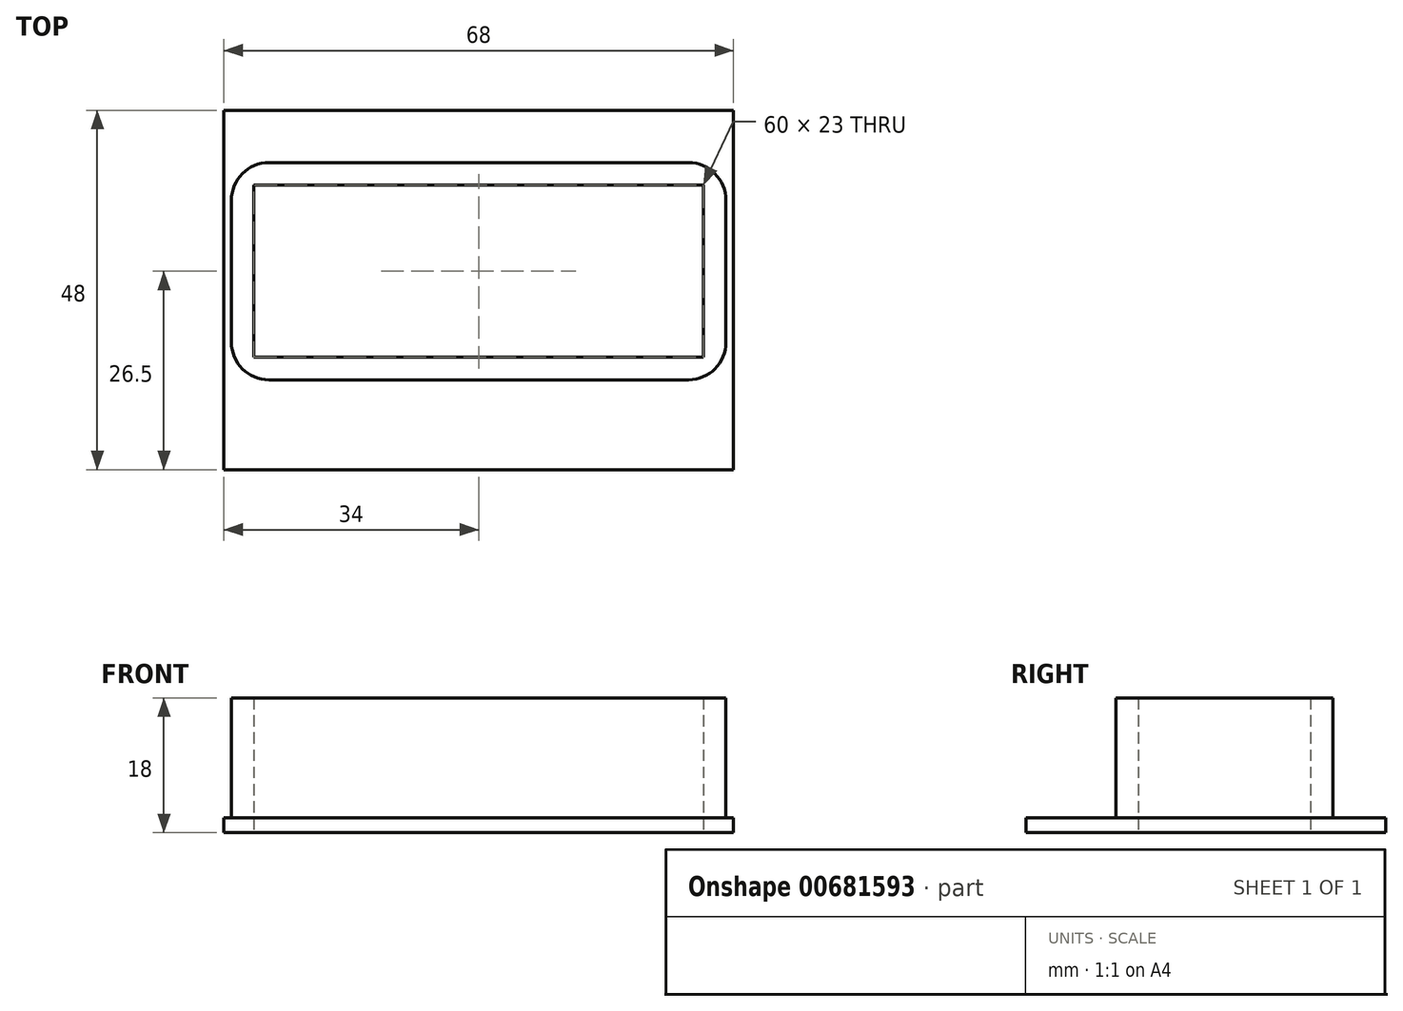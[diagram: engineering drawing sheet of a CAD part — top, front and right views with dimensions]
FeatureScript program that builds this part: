
annotation { "Feature Type Name" : "Feature", "Feature Type Description" : "" }
export const myFeature = defineFeature(function(context is Context, id is Id, definition is map)
    precondition{}
    {
        {
            var Q0;
            Q0=qCreatedBy(makeId("Top.planeOp"),FACE);
            var sketch = newSketch(context, id + "F0", { "sketchPlane" : qUnion([Q0])});
            skLineSegment(sketch, "E0.bottom", {"start": v(5, 0) * mm, "end": v(61, 0) * mm});
            skLineSegment(sketch, "E0.top", {"start": v(5, 29) * mm, "end": v(61, 29) * mm});
            skLineSegment(sketch, "E0.left", {"start": v(0, 5) * mm, "end": v(0, 24) * mm});
            skLineSegment(sketch, "E0.right", {"start": v(66, 5) * mm, "end": v(66, 24) * mm});
            skPoint(sketch, "E1.visualSharp", {"position": v(0, 29) * mm});
            skArc(sketch, "E1.filletArc", {"start": v(5, 29) * mm, "mid": v(1.46, 27.54) * mm, "end": v(0, 24) * mm});
            skPoint(sketch, "E2.visualSharp", {"position": v(0, 0) * mm});
            skArc(sketch, "E2.filletArc", {"start": v(0, 5) * mm, "mid": v(1.46, 1.46) * mm, "end": v(5, 0) * mm});
            skPoint(sketch, "E3.visualSharp", {"position": v(66, 0) * mm});
            skArc(sketch, "E3.filletArc", {"start": v(61, 0) * mm, "mid": v(64.54, 1.46) * mm, "end": v(66, 5) * mm});
            skPoint(sketch, "E4.visualSharp", {"position": v(66, 29) * mm});
            skArc(sketch, "E4.filletArc", {"start": v(66, 24) * mm, "mid": v(64.54, 27.54) * mm, "end": v(61, 29) * mm});
            skLineSegment(sketch, "E5.bottom", {"start": v(67, -12) * mm, "end": v(-1, -12) * mm});
            skLineSegment(sketch, "E5.top", {"start": v(67, 36) * mm, "end": v(-1, 36) * mm});
            skLineSegment(sketch, "E5.left", {"start": v(67, -12) * mm, "end": v(67, 36) * mm});
            skLineSegment(sketch, "E5.right", {"start": v(-1, -12) * mm, "end": v(-1, 36) * mm});
            skPoint(sketch, "E5.middle", {"position": v(33, 14.5) * mm});
            skLineSegment(sketch, "E6.bottom", {"start": v(63, 3) * mm, "end": v(3, 3) * mm});
            skLineSegment(sketch, "E6.top", {"start": v(63, 26) * mm, "end": v(3, 26) * mm});
            skLineSegment(sketch, "E6.left", {"start": v(63, 3) * mm, "end": v(63, 26) * mm});
            skLineSegment(sketch, "E6.right", {"start": v(3, 3) * mm, "end": v(3, 26) * mm});
            skPoint(sketch, "E7.start.orphan", {"position": v(0, 14.5) * mm});
            skPoint(sketch, "E8.start.orphan", {"position": v(33, 29) * mm});
            skPoint(sketch, "E9.trimOffspring.end.orphan", {"position": v(33, 0) * mm});
            skPoint(sketch, "E10.trimOffspring.end.orphan", {"position": v(66, 14.5) * mm});
            skSolve(sketch);
        }
        {
            var Q0;
            Q0=makeQuery(id+"F0.imprint","IMPRINT",FACE,{"disambiguationData":[TD([[makeQuery(id+"F0.imprint","IMPRINT",EDGE,{"derivedFrom":sQuery(id+"F0.wireOp",EDGE,"E0.bottom")}),-1.0]])]});
            extrude(context, id + "F1", {"entities" : qUnion([Q0]), "depth" : 2 * mm, "offsetDistance" : 25 * mm});
        }
        {
            var Q0;
            Q0=makeQuery(id+"F0.imprint","IMPRINT",FACE,{"disambiguationData":[TD([[makeQuery(id+"F0.imprint","IMPRINT",EDGE,{"derivedFrom":sQuery(id+"F0.wireOp",EDGE,"E0.bottom")}),1.0]])]});
            extrude(context, id + "F2", {"entities" : qUnion([Q0]), "operationType" : NewBodyOperationType.ADD, "depth" : 18 * mm, "offsetDistance" : 25 * mm});
        }
    });
